annotation { "Feature Type Name" : "Feature", "Feature Type Description" : "" }
export const myFeature = defineFeature(function(context is Context, id is Id, definition is map)
    precondition{}
    {
        {
            var Q0;
            Q0=qCreatedBy(makeId("Top.planeOp"),FACE);
            var sketch = newSketch(context, id + "F0", { "sketchPlane" : qUnion([Q0])});
            skLineSegment(sketch, "E0.bottom", {"start": v(0, 0) * mm, "end": v(2000, 0) * mm});
            skLineSegment(sketch, "E0.top", {"start": v(0, 2000) * mm, "end": v(2000, 2000) * mm});
            skLineSegment(sketch, "E0.left", {"start": v(0, 0) * mm, "end": v(0, 2000) * mm});
            skLineSegment(sketch, "E0.right", {"start": v(2000, 0) * mm, "end": v(2000, 2000) * mm});
            skSolve(sketch);
        }
        {
            var Q0;
            Q0=makeQuery(id+"F0.imprint","IMPRINT",FACE,{"disambiguationData":[TD([[makeQuery(id+"F0.imprint","IMPRINT",EDGE,{"derivedFrom":sQuery(id+"F0.wireOp",EDGE,"E0.bottom")}),1.0]])]});
            extrude(context, id + "F1", {"entities" : qUnion([Q0]), "oppositeDirection" : true, "depth" : 500 * mm, "offsetDistance" : 25 * mm});
        }
        {
            var Q0;
            Q0=makeQuery(id+"F1.opExtrude","CAP_FACE",FACE,{"disambiguationData":[OSD([sQuery(id+"F0.wireOp",EDGE,"E0.bottom"),sQuery(id+"F0.wireOp",EDGE,"E0.top"),sQuery(id+"F0.wireOp",EDGE,"E0.left"),sQuery(id+"F0.wireOp",EDGE,"E0.right")])],"isStart":true});
            cPlane(context, id + "F2", {"entities" : qUnion([Q0]), "cplaneType" : CPlaneType.OFFSET, "offset" : 1500 * mm, "width" : 150 * mm, "height" : 150 * mm});
        }
        {
            var Q0;
            Q0=qCreatedBy(id+"F2.planeOp",FACE);
            var sketch = newSketch(context, id + "F3", { "sketchPlane" : qUnion([Q0])});
            skLineSegment(sketch, "E1.bottom", {"start": v(0, 1500) * mm, "end": v(2000, 1500) * mm});
            skLineSegment(sketch, "E1.top", {"start": v(0, -500) * mm, "end": v(2000, -500) * mm});
            skLineSegment(sketch, "E1.left", {"start": v(0, 1500) * mm, "end": v(0, -500) * mm});
            skLineSegment(sketch, "E1.right", {"start": v(2000, 1500) * mm, "end": v(2000, -500) * mm});
            skSolve(sketch);
        }
        {
            var Q1;
            Q1=makeQuery(id+"F3.imprint","IMPRINT",FACE,{"disambiguationData":[TD([[makeQuery(id+"F3.imprint","IMPRINT",EDGE,{"derivedFrom":sQuery(id+"F3.wireOp",EDGE,"E1.bottom")}),-1.0]])]});
            var Q2;
            Q2=makeQuery(id+"F1.opExtrude","CAP_FACE",FACE,{"disambiguationData":[OSD([sQuery(id+"F0.wireOp",EDGE,"E0.bottom"),sQuery(id+"F0.wireOp",EDGE,"E0.top"),sQuery(id+"F0.wireOp",EDGE,"E0.left"),sQuery(id+"F0.wireOp",EDGE,"E0.right")])],"isStart":true});
            loft(context, id + "F4", {"operationType" : NewBodyOperationType.ADD, "sheetProfilesArray" : [{ "sheetProfileEntities" : qUnion([Q1]) }, { "sheetProfileEntities" : qUnion([Q2]) }]});
        }
        {
            var Q0;
            Q0=makeQuery(id+"F1.opExtrude","CAP_FACE",FACE,{"disambiguationData":[OSD([sQuery(id+"F0.wireOp",EDGE,"E0.bottom"),sQuery(id+"F0.wireOp",EDGE,"E0.top"),sQuery(id+"F0.wireOp",EDGE,"E0.left"),sQuery(id+"F0.wireOp",EDGE,"E0.right")])],"isStart":false});
            cPlane(context, id + "F5", {"entities" : qUnion([Q0]), "cplaneType" : CPlaneType.OFFSET, "offset" : 1200 * mm, "width" : 150 * mm, "height" : 150 * mm});
        }
        {
            var Q0;
            Q0=qCreatedBy(id+"F5.planeOp",FACE);
            var sketch = newSketch(context, id + "F6", { "sketchPlane" : qUnion([Q0])});
            skLineSegment(sketch, "E2.bottom", {"start": v(900, -900) * mm, "end": v(1100, -900) * mm});
            skLineSegment(sketch, "E2.top", {"start": v(900, -1100) * mm, "end": v(1100, -1100) * mm});
            skLineSegment(sketch, "E2.left", {"start": v(900, -900) * mm, "end": v(900, -1100) * mm});
            skLineSegment(sketch, "E2.right", {"start": v(1100, -900) * mm, "end": v(1100, -1100) * mm});
            skSolve(sketch);
        }
        {
            var Q1;
            Q1=makeQuery(id+"F1.opExtrude","CAP_FACE",FACE,{"disambiguationData":[OSD([sQuery(id+"F0.wireOp",EDGE,"E0.bottom"),sQuery(id+"F0.wireOp",EDGE,"E0.top"),sQuery(id+"F0.wireOp",EDGE,"E0.left"),sQuery(id+"F0.wireOp",EDGE,"E0.right")])],"isStart":false});
            var Q2;
            Q2=makeQuery(id+"F6.imprint","IMPRINT",FACE,{"disambiguationData":[TD([[makeQuery(id+"F6.imprint","IMPRINT",EDGE,{"derivedFrom":sQuery(id+"F6.wireOp",EDGE,"E2.bottom")}),-1.0]])]});
            loft(context, id + "F7", {"operationType" : NewBodyOperationType.ADD, "sheetProfilesArray" : [{ "sheetProfileEntities" : qUnion([Q1]) }, { "sheetProfileEntities" : qUnion([Q2]) }]});
        }
        {
            var Q0;
            Q0=makeQuery(id+"F4.opLoft","CAP_FACE",FACE,{"disambiguationData":[OSD([makeQuery(id+"F3.imprint","IMPRINT",FACE,{"disambiguationData":[TD([[makeQuery(id+"F3.imprint","IMPRINT",EDGE,{"derivedFrom":sQuery(id+"F3.wireOp",EDGE,"E1.bottom")}),-1.0]])]})])],"isStart":true});
            var sketch = newSketch(context, id + "F8", { "sketchPlane" : qUnion([Q0])});
            skLineSegment(sketch, "E3.bottom", {"start": v(2000, -500) * mm, "end": v(0, -500) * mm});
            skLineSegment(sketch, "E3.top", {"start": v(2000, 1800) * mm, "end": v(0, 1800) * mm});
            skLineSegment(sketch, "E3.left", {"start": v(2000, -500) * mm, "end": v(2000, 1800) * mm});
            skLineSegment(sketch, "E3.right", {"start": v(0, -500) * mm, "end": v(0, 1800) * mm});
            skSolve(sketch);
        }
        {
            var Q0;
            Q0 = qSketchRegion(id + "F8", true);
            extrude(context, id + "F9", {"entities" : qUnion([Q0]), "operationType" : NewBodyOperationType.ADD, "depth" : 300 * mm, "offsetDistance" : 25 * mm});
        }
        {
            var Q0;
            Q0=makeQuery(id+"F9.opExtrude","SWEPT_FACE",FACE,{"disambiguationData":[OSD([sQuery(id+"F8.wireOp",EDGE,"E3.top")])]});
            var sketch = newSketch(context, id + "F10", { "sketchPlane" : qUnion([Q0])});
            skCircle(sketch, "E4", {"center": v(-1000, 1650) * mm, "radius": 50 * mm});
            skPoint(sketch, "E4.centerSnap0", {"position": v(-1000, 1800) * mm});
            skSolve(sketch);
        }
        {
            var Q0;
            Q0=makeQuery(id+"F10.imprint","IMPRINT",FACE,{"disambiguationData":[TD([[makeQuery(id+"F10.imprint","IMPRINT",EDGE,{"derivedFrom":sQuery(id+"F10.wireOp",EDGE,"E4")}),1.0]])]});
            var Q1;
            Q1=sQuery(id+"F10.wireOp",EDGE,"E4");
            extrude(context, id + "F11", {"entities" : qUnion([Q0]), "operationType" : NewBodyOperationType.ADD, "surfaceEntities" : qUnion([Q1]), "depth" : 100 * mm, "offsetDistance" : 25 * mm});
        }
        {
            var Q0;
            Q0=makeQuery(id+"F11.opExtrude","CAP_FACE",FACE,{"disambiguationData":[OSD([sQuery(id+"F10.wireOp",EDGE,"E4")])],"isStart":false});
            var sketch = newSketch(context, id + "F12", { "sketchPlane" : qUnion([Q0])});
            skCircle(sketch, "E5", {"center": v(-1000, 1650) * mm, "radius": 115 * mm});
            skCircle(sketch, "E6", {"center": v(-1000, 1745) * mm, "radius": 9 * mm});
            skCircle(sketch, "E7.1.0", {"center": v(-1067.18, 1717.18) * mm, "radius": 9 * mm});
            skCircle(sketch, "E7.2.0", {"center": v(-1095, 1650) * mm, "radius": 9 * mm});
            skCircle(sketch, "E7.3.0", {"center": v(-1067.18, 1582.82) * mm, "radius": 9 * mm});
            skCircle(sketch, "E7.4.0", {"center": v(-1000, 1555) * mm, "radius": 9 * mm});
            skCircle(sketch, "E7.5.0", {"center": v(-932.82, 1582.82) * mm, "radius": 9 * mm});
            skCircle(sketch, "E7.6.0", {"center": v(-905, 1650) * mm, "radius": 9 * mm});
            skCircle(sketch, "E7.7.0", {"center": v(-932.82, 1717.18) * mm, "radius": 9 * mm});
            skSolve(sketch);
        }
        {
            var Q0;
            Q0=makeQuery(id+"F12.imprint","IMPRINT",FACE,{"disambiguationData":[TD([[makeQuery(id+"F12.imprint","IMPRINT",EDGE,{"derivedFrom":sQuery(id+"F12.wireOp",EDGE,"E5")}),1.0]])]});
            extrude(context, id + "F13", {"entities" : qUnion([Q0]), "operationType" : NewBodyOperationType.ADD, "oppositeDirection" : true, "depth" : 25 * mm, "offsetDistance" : 25 * mm});
        }
        {
            var Q0;
            {var subQ0=sQuery(id+"F10.wireOp",EDGE,"E4");Q0=makeQuery(id+"F13.boolean.opBoolean","MERGE",FACE,{"derivedFrom":[makeQuery(id+"F11.opExtrude","CAP_FACE",FACE,{"disambiguationData":[OSD([subQ0])],"isStart":false}),makeQuery(id+"F13.opExtrude","CAP_FACE",FACE,{"disambiguationData":[OSD([subQ0,sQuery(id+"F12.wireOp",EDGE,"E5"),sQuery(id+"F12.wireOp",EDGE,"E6"),sQuery(id+"F12.wireOp",EDGE,"E7.1.0"),sQuery(id+"F12.wireOp",EDGE,"E7.2.0"),sQuery(id+"F12.wireOp",EDGE,"E7.3.0"),sQuery(id+"F12.wireOp",EDGE,"E7.4.0"),sQuery(id+"F12.wireOp",EDGE,"E7.5.0"),sQuery(id+"F12.wireOp",EDGE,"E7.6.0"),sQuery(id+"F12.wireOp",EDGE,"E7.7.0")])],"isStart":true})]});}
            var sketch = newSketch(context, id + "F14", { "sketchPlane" : qUnion([Q0])});
            skCircle(sketch, "E8", {"center": v(-1000, 1650) * mm, "radius": 40 * mm});
            skSolve(sketch);
        }
        {
            var Q0;
            Q0=makeQuery(id+"F14.imprint","IMPRINT",FACE,{"disambiguationData":[TD([[makeQuery(id+"F14.imprint","IMPRINT",EDGE,{"derivedFrom":sQuery(id+"F14.wireOp",EDGE,"E8")}),1.0]])]});
            extrude(context, id + "F15", {"entities" : qUnion([Q0]), "operationType" : NewBodyOperationType.REMOVE, "oppositeDirection" : true, "depth" : 500 * mm, "offsetDistance" : 25 * mm});
        }
        {
            var Q0;
            Q0=makeQuery(id+"F1.opExtrude","SWEPT_FACE",FACE,{"disambiguationData":[OSD([sQuery(id+"F0.wireOp",EDGE,"E0.top")])]});
            var sketch = newSketch(context, id + "F16", { "sketchPlane" : qUnion([Q0])});
            skCircle(sketch, "E9", {"center": v(-1000, -250) * mm, "radius": 40 * mm});
            skCircle(sketch, "E10", {"center": v(-1000, -250) * mm, "radius": 50 * mm});
            skSolve(sketch);
        }
        {
            var Q0;
            Q0=makeQuery(id+"F16.imprint","IMPRINT",FACE,{"disambiguationData":[TD([[makeQuery(id+"F16.imprint","IMPRINT",EDGE,{"derivedFrom":sQuery(id+"F16.wireOp",EDGE,"E9")}),1.0]])]});
            extrude(context, id + "F17", {"entities" : qUnion([Q0]), "operationType" : NewBodyOperationType.REMOVE, "oppositeDirection" : true, "depth" : 25 * mm, "offsetDistance" : 25 * mm});
        }
        {
            var Q0;
            Q0 = qSketchRegion(id + "F16", true);
            extrude(context, id + "F18", {"entities" : qUnion([Q0]), "operationType" : NewBodyOperationType.ADD, "depth" : 100 * mm, "offsetDistance" : 25 * mm});
        }
        {
            var Q0;
            Q0=makeQuery(id+"F18.opExtrude","CAP_FACE",FACE,{"disambiguationData":[OSD([sQuery(id+"F16.wireOp",EDGE,"E9"),sQuery(id+"F16.wireOp",EDGE,"E10")])],"isStart":false});
            var sketch = newSketch(context, id + "F19", { "sketchPlane" : qUnion([Q0])});
            skCircle(sketch, "E11", {"center": v(-1000, -250) * mm, "radius": 100 * mm});
            skCircle(sketch, "E12", {"center": v(-1000, -173) * mm, "radius": 8 * mm});
            skCircle(sketch, "E13.1.0", {"center": v(-1054.45, -195.55) * mm, "radius": 8 * mm});
            skCircle(sketch, "E13.2.0", {"center": v(-1077, -250) * mm, "radius": 8 * mm});
            skCircle(sketch, "E13.3.0", {"center": v(-1054.45, -304.45) * mm, "radius": 8 * mm});
            skCircle(sketch, "E13.4.0", {"center": v(-1000, -327) * mm, "radius": 8 * mm});
            skCircle(sketch, "E13.5.0", {"center": v(-945.55, -304.45) * mm, "radius": 8 * mm});
            skCircle(sketch, "E13.6.0", {"center": v(-923, -250) * mm, "radius": 8 * mm});
            skCircle(sketch, "E13.7.0", {"center": v(-945.55, -195.55) * mm, "radius": 8 * mm});
            skSolve(sketch);
        }
        {
            var Q0;
            Q0=makeQuery(id+"F19.imprint","IMPRINT",FACE,{"disambiguationData":[TD([[makeQuery(id+"F19.imprint","IMPRINT",EDGE,{"derivedFrom":sQuery(id+"F19.wireOp",EDGE,"E11")}),1.0]])]});
            extrude(context, id + "F20", {"entities" : qUnion([Q0]), "operationType" : NewBodyOperationType.ADD, "oppositeDirection" : true, "depth" : 15 * mm, "offsetDistance" : 25 * mm});
        }
        {
            var Q0;
            {var subQ0=sQuery(id+"F0.wireOp",EDGE,"E0.left");Q0=makeQuery(id+"F9.boolean.opBoolean","MERGE",FACE,{"derivedFrom":[makeQuery(id+"F4.boolean.opBoolean","MERGE",FACE,{"derivedFrom":[makeQuery(id+"F1.opExtrude","SWEPT_FACE",FACE,{"disambiguationData":[OSD([subQ0])]}),makeQuery(id+"F4.opLoft","SWEPT_FACE",FACE,{"disambiguationData":[OSD([sQuery(id+"F0.wireOp",EDGE,"E0.bottom"),sQuery(id+"F0.wireOp",EDGE,"E0.top"),subQ0,sQuery(id+"F3.wireOp",EDGE,"E1.bottom"),sQuery(id+"F3.wireOp",EDGE,"E1.top"),sQuery(id+"F3.wireOp",EDGE,"E1.left")])]})]}),makeQuery(id+"F9.opExtrude","SWEPT_FACE",FACE,{"disambiguationData":[OSD([sQuery(id+"F8.wireOp",EDGE,"E3.right")])]})]});}
            var sketch = newSketch(context, id + "F21", { "sketchPlane" : qUnion([Q0])});
            skLineSegment(sketch, "E14.bottom", {"start": v(-2050, 0) * mm, "end": v(50, 0) * mm});
            skLineSegment(sketch, "E14.top", {"start": v(-2050, -10) * mm, "end": v(50, -10) * mm});
            skLineSegment(sketch, "E14.left", {"start": v(-2050, 0) * mm, "end": v(-2050, -10) * mm});
            skLineSegment(sketch, "E14.right", {"start": v(50, 0) * mm, "end": v(50, -10) * mm});
            skLineSegment(sketch, "E15.0.1.0", {"start": v(-2050, -490) * mm, "end": v(50, -490) * mm});
            skLineSegment(sketch, "E15.0.1.1", {"start": v(-2050, -500) * mm, "end": v(50, -500) * mm});
            skLineSegment(sketch, "E15.0.1.2", {"start": v(50, -490) * mm, "end": v(50, -500) * mm});
            skLineSegment(sketch, "E15.0.1.3", {"start": v(-2050, -490) * mm, "end": v(-2050, -500) * mm});
            skLineSegment(sketch, "E15.direction1", {"start": v(-2050, 0) * mm, "end": v(-2025, 0) * mm, "construction": true});
            skLineSegment(sketch, "E15.direction2", {"start": v(-2050, 0) * mm, "end": v(-2050, -490) * mm, "construction": true});
            skSolve(sketch);
        }
        {
            var Q0;
            Q0 = qSketchRegion(id + "F21", true);
            extrude(context, id + "F22", {"entities" : qUnion([Q0]), "operationType" : NewBodyOperationType.ADD, "oppositeDirection" : true, "depth" : 2050 * mm, "offsetDistance" : 25 * mm, "hasSecondDirection" : true, "secondDirectionOppositeDirection" : false, "secondDirectionDepth" : 50 * mm});
        }
        {
            var Q0;
            {var subQ0=sQuery(id+"F8.wireOp",EDGE,"E3.bottom");var subQ2=sQuery(id+"F3.wireOp",EDGE,"E1.left");var subQ3=sQuery(id+"F3.wireOp",EDGE,"E1.bottom");var subQ5=sQuery(id+"F0.wireOp",EDGE,"E0.left");var subQ6=sQuery(id+"F0.wireOp",EDGE,"E0.top");var subQ7=sQuery(id+"F8.wireOp",EDGE,"E3.right");var subQ10=sQuery(id+"F3.wireOp",EDGE,"E1.top");var subQ11=sQuery(id+"F0.wireOp",EDGE,"E0.bottom");Q0=makeQuery(id+"F22.boolean.opBoolean","SPLIT",FACE,{"disambiguationData":[TD([makeQuery(id+"F9.opExtrude","SWEPT_FACE",FACE,{"disambiguationData":[OSD([subQ0])]})])],"derivedFrom":makeQuery(id+"F9.boolean.opBoolean","MERGE",FACE,{"derivedFrom":[makeQuery(id+"F4.boolean.opBoolean","MERGE",FACE,{"derivedFrom":[makeQuery(id+"F1.opExtrude","SWEPT_FACE",FACE,{"disambiguationData":[OSD([subQ5])]}),makeQuery(id+"F4.opLoft","SWEPT_FACE",FACE,{"disambiguationData":[OSD([subQ11,subQ6,subQ5,subQ3,subQ10,subQ2])]})]}),makeQuery(id+"F9.opExtrude","SWEPT_FACE",FACE,{"disambiguationData":[OSD([subQ7])]})]})});}
            var sketch = newSketch(context, id + "F23", { "sketchPlane" : qUnion([Q0])});
            skLineSegment(sketch, "E16.0", {"start": v(-1500, 1500) * mm, "end": v(-2000, 0) * mm});
            skLineSegment(sketch, "E17", {"start": v(-1500, 1500) * mm, "end": v(-1480, 1500) * mm});
            skLineSegment(sketch, "E18", {"start": v(-1480, 1500) * mm, "end": v(-1980, 0) * mm});
            skLineSegment(sketch, "E19", {"start": v(-1980, 0) * mm, "end": v(-2000, 0) * mm});
            skLineSegment(sketch, "E20.1.0.0", {"start": v(-820, 1500) * mm, "end": v(-1320, 0) * mm});
            skLineSegment(sketch, "E20.1.0.1", {"start": v(-840, 1500) * mm, "end": v(-1340, 0) * mm});
            skLineSegment(sketch, "E20.1.0.2", {"start": v(-840, 1500) * mm, "end": v(-820, 1500) * mm});
            skLineSegment(sketch, "E20.1.0.3", {"start": v(-1320, 0) * mm, "end": v(-1340, 0) * mm});
            skLineSegment(sketch, "E20.2.0.0", {"start": v(-160, 1500) * mm, "end": v(-660, 0) * mm});
            skLineSegment(sketch, "E20.2.0.1", {"start": v(-180, 1500) * mm, "end": v(-680, 0) * mm});
            skLineSegment(sketch, "E20.2.0.2", {"start": v(-180, 1500) * mm, "end": v(-160, 1500) * mm});
            skLineSegment(sketch, "E20.2.0.3", {"start": v(-660, 0) * mm, "end": v(-680, 0) * mm});
            skLineSegment(sketch, "E20.3.0.0", {"start": v(500, 1500) * mm, "end": v(0, 0) * mm});
            skLineSegment(sketch, "E20.3.0.1", {"start": v(480, 1500) * mm, "end": v(-20, 0) * mm});
            skLineSegment(sketch, "E20.3.0.2", {"start": v(480, 1500) * mm, "end": v(500, 1500) * mm});
            skLineSegment(sketch, "E20.3.0.3", {"start": v(0, 0) * mm, "end": v(-20, 0) * mm});
            skLineSegment(sketch, "E20.direction1", {"start": v(-1980, 0) * mm, "end": v(-1320, 0) * mm, "construction": true});
            skSolve(sketch);
        }
        {
            var Q0;
            Q0 = qSketchRegion(id + "F23", true);
            extrude(context, id + "F24", {"entities" : qUnion([Q0]), "operationType" : NewBodyOperationType.ADD, "oppositeDirection" : true, "depth" : 2050 * mm, "offsetDistance" : 25 * mm, "hasSecondDirection" : true, "secondDirectionOppositeDirection" : false, "secondDirectionDepth" : 50 * mm});
        }
        {
            var Q0;
            {var subQ0=sQuery(id+"F8.wireOp",EDGE,"E3.bottom");var subQ2=sQuery(id+"F3.wireOp",EDGE,"E1.left");var subQ3=sQuery(id+"F3.wireOp",EDGE,"E1.bottom");var subQ5=sQuery(id+"F0.wireOp",EDGE,"E0.left");var subQ6=sQuery(id+"F0.wireOp",EDGE,"E0.top");var subQ7=sQuery(id+"F8.wireOp",EDGE,"E3.right");var subQ10=sQuery(id+"F3.wireOp",EDGE,"E1.top");var subQ11=sQuery(id+"F0.wireOp",EDGE,"E0.bottom");Q0=makeQuery(id+"F22.boolean.opBoolean","SPLIT",FACE,{"disambiguationData":[TD([makeQuery(id+"F9.opExtrude","SWEPT_FACE",FACE,{"disambiguationData":[OSD([subQ0])]})])],"derivedFrom":makeQuery(id+"F9.boolean.opBoolean","MERGE",FACE,{"derivedFrom":[makeQuery(id+"F4.boolean.opBoolean","MERGE",FACE,{"derivedFrom":[makeQuery(id+"F1.opExtrude","SWEPT_FACE",FACE,{"disambiguationData":[OSD([subQ5])]}),makeQuery(id+"F4.opLoft","SWEPT_FACE",FACE,{"disambiguationData":[OSD([subQ11,subQ6,subQ5,subQ3,subQ10,subQ2])]})]}),makeQuery(id+"F9.opExtrude","SWEPT_FACE",FACE,{"disambiguationData":[OSD([subQ7])]})]})});}
            var sketch = newSketch(context, id + "F25", { "sketchPlane" : qUnion([Q0])});
            skLineSegment(sketch, "E21.bottom", {"start": v(500, 1500) * mm, "end": v(-1850, 1500) * mm});
            skLineSegment(sketch, "E21.top", {"start": v(500, 1520) * mm, "end": v(-1850, 1520) * mm});
            skLineSegment(sketch, "E21.left", {"start": v(500, 1500) * mm, "end": v(500, 1520) * mm});
            skLineSegment(sketch, "E21.right", {"start": v(-1850, 1500) * mm, "end": v(-1850, 1520) * mm});
            skSolve(sketch);
        }
        {
            var Q0;
            Q0 = qSketchRegion(id + "F25", true);
            extrude(context, id + "F26", {"entities" : qUnion([Q0]), "operationType" : NewBodyOperationType.ADD, "oppositeDirection" : true, "depth" : 2050 * mm, "offsetDistance" : 25 * mm, "hasSecondDirection" : true, "secondDirectionOppositeDirection" : false, "secondDirectionDepth" : 50 * mm});
        }
        {
            var Q0;
            Q0=makeQuery(id+"F7.opLoft","CAP_FACE",FACE,{"disambiguationData":[OSD([makeQuery(id+"F6.imprint","IMPRINT",FACE,{"disambiguationData":[TD([[makeQuery(id+"F6.imprint","IMPRINT",EDGE,{"derivedFrom":sQuery(id+"F6.wireOp",EDGE,"E2.bottom")}),-1.0]])]})])],"isStart":true});
            cPlane(context, id + "F27", {"entities" : qUnion([Q0]), "cplaneType" : CPlaneType.OFFSET, "offset" : 400 * mm, "oppositeDirection" : true, "width" : 150 * mm, "height" : 150 * mm});
        }
        {
            var Q0;
            Q0=makeQuery(id+"F7.opLoft","CAP_FACE",FACE,{"disambiguationData":[OSD([makeQuery(id+"F6.imprint","IMPRINT",FACE,{"disambiguationData":[TD([[makeQuery(id+"F6.imprint","IMPRINT",EDGE,{"derivedFrom":sQuery(id+"F6.wireOp",EDGE,"E2.bottom")}),-1.0]])]})])],"isStart":true});
            cPlane(context, id + "F28", {"entities" : qUnion([Q0]), "cplaneType" : CPlaneType.OFFSET, "offset" : 800 * mm, "oppositeDirection" : true, "width" : 150 * mm, "height" : 150 * mm});
        }
        {
            var Q0;
            Q0=qCreatedBy(id+"F27.planeOp",FACE);
            var sketch = newSketch(context, id + "F29", { "sketchPlane" : qUnion([Q0])});
            skLineSegment(sketch, "E22.bottom", {"start": v(503.12, -1496.88) * mm, "end": v(1503.12, -1496.88) * mm});
            skLineSegment(sketch, "E22.top", {"start": v(503.12, -496.88) * mm, "end": v(1503.12, -496.88) * mm});
            skLineSegment(sketch, "E22.left", {"start": v(503.12, -1496.88) * mm, "end": v(503.12, -496.88) * mm});
            skLineSegment(sketch, "E22.right", {"start": v(1503.12, -1496.88) * mm, "end": v(1503.12, -496.88) * mm});
            skLineSegment(sketch, "E23.0", {"start": v(0, -2000) * mm, "end": v(900, -1100) * mm});
            skLineSegment(sketch, "E24.0", {"start": v(0, 0) * mm, "end": v(900, -900) * mm});
            skSolve(sketch);
        }
        {
            var Q0;
            Q0 = qSketchRegion(id + "F29", true);
            extrude(context, id + "F30", {"entities" : qUnion([Q0]), "operationType" : NewBodyOperationType.ADD, "oppositeDirection" : true, "depth" : 25 * mm, "offsetDistance" : 25 * mm});
        }
        {
            var Q0;
            Q0=qCreatedBy(id+"F28.planeOp",FACE);
            var sketch = newSketch(context, id + "F31", { "sketchPlane" : qUnion([Q0])});
            skLineSegment(sketch, "E25.bottom", {"start": v(251.64, -1748.81) * mm, "end": v(1751.64, -1748.81) * mm});
            skLineSegment(sketch, "E25.top", {"start": v(251.64, -248.81) * mm, "end": v(1751.64, -248.81) * mm});
            skLineSegment(sketch, "E25.left", {"start": v(251.64, -1748.81) * mm, "end": v(251.64, -248.81) * mm});
            skLineSegment(sketch, "E25.right", {"start": v(1751.64, -1748.81) * mm, "end": v(1751.64, -248.81) * mm});
            skSolve(sketch);
        }
        {
            var Q0;
            Q0 = qSketchRegion(id + "F31", true);
            extrude(context, id + "F32", {"entities" : qUnion([Q0]), "operationType" : NewBodyOperationType.ADD, "depth" : 25 * mm, "offsetDistance" : 25 * mm});
        }
        {
            var Q0;
            Q0=makeQuery(id+"F22.opExtrude","SWEPT_FACE",FACE,{"disambiguationData":[OSD([sQuery(id+"F21.wireOp",EDGE,"E15.0.1.1")])]});
            var sketch = newSketch(context, id + "F33", { "sketchPlane" : qUnion([Q0])});
            skLineSegment(sketch, "E26.bottom", {"start": v(-50, -2050) * mm, "end": v(70, -2050) * mm});
            skLineSegment(sketch, "E26.top", {"start": v(-50, -1930) * mm, "end": v(70, -1930) * mm});
            skLineSegment(sketch, "E26.left", {"start": v(-50, -2050) * mm, "end": v(-50, -1930) * mm});
            skLineSegment(sketch, "E26.right", {"start": v(70, -2050) * mm, "end": v(70, -1930) * mm});
            skLineSegment(sketch, "E27.0.1.0", {"start": v(-50, 50) * mm, "end": v(70, 50) * mm});
            skLineSegment(sketch, "E27.0.1.1", {"start": v(70, -70) * mm, "end": v(70, 50) * mm});
            skLineSegment(sketch, "E27.0.1.2", {"start": v(-50, -70) * mm, "end": v(70, -70) * mm});
            skLineSegment(sketch, "E27.0.1.3", {"start": v(-50, -70) * mm, "end": v(-50, 50) * mm});
            skLineSegment(sketch, "E27.1.0.0", {"start": v(1930, -1930) * mm, "end": v(2050, -1930) * mm});
            skLineSegment(sketch, "E27.1.0.1", {"start": v(2050, -2050) * mm, "end": v(2050, -1930) * mm});
            skLineSegment(sketch, "E27.1.0.2", {"start": v(1930, -2050) * mm, "end": v(2050, -2050) * mm});
            skLineSegment(sketch, "E27.1.0.3", {"start": v(1930, -2050) * mm, "end": v(1930, -1930) * mm});
            skLineSegment(sketch, "E27.1.1.0", {"start": v(1930, 50) * mm, "end": v(2050, 50) * mm});
            skLineSegment(sketch, "E27.1.1.1", {"start": v(2050, -70) * mm, "end": v(2050, 50) * mm});
            skLineSegment(sketch, "E27.1.1.2", {"start": v(1930, -70) * mm, "end": v(2050, -70) * mm});
            skLineSegment(sketch, "E27.1.1.3", {"start": v(1930, -70) * mm, "end": v(1930, 50) * mm});
            skLineSegment(sketch, "E27.direction1", {"start": v(-50, -1930) * mm, "end": v(1930, -1930) * mm, "construction": true});
            skLineSegment(sketch, "E27.direction2", {"start": v(-50, -1930) * mm, "end": v(-50, 50) * mm, "construction": true});
            skSolve(sketch);
        }
        {
            var Q0;
            Q0 = qSketchRegion(id + "F33", true);
            extrude(context, id + "F34", {"entities" : qUnion([Q0]), "operationType" : NewBodyOperationType.ADD, "depth" : 1800 * mm, "offsetDistance" : 25 * mm});
        }
        {
            var Q0;
            Q0=makeQuery(id+"F7.opLoft","CAP_FACE",FACE,{"disambiguationData":[OSD([makeQuery(id+"F6.imprint","IMPRINT",FACE,{"disambiguationData":[TD([[makeQuery(id+"F6.imprint","IMPRINT",EDGE,{"derivedFrom":sQuery(id+"F6.wireOp",EDGE,"E2.bottom")}),-1.0]])]})])],"isStart":true});
            var sketch = newSketch(context, id + "F35", { "sketchPlane" : qUnion([Q0])});
            skLineSegment(sketch, "E28.bottom", {"start": v(900, -1100) * mm, "end": v(1100, -1100) * mm});
            skLineSegment(sketch, "E28.top", {"start": v(900, -900) * mm, "end": v(1100, -900) * mm});
            skLineSegment(sketch, "E28.left", {"start": v(900, -1100) * mm, "end": v(900, -900) * mm});
            skLineSegment(sketch, "E28.right", {"start": v(1100, -1100) * mm, "end": v(1100, -900) * mm});
            skSolve(sketch);
        }
        {
            var Q0;
            Q0=makeQuery(id+"F35.imprint","IMPRINT",FACE,{"disambiguationData":[TD([[makeQuery(id+"F35.imprint","IMPRINT",EDGE,{"derivedFrom":sQuery(id+"F35.wireOp",EDGE,"E28.bottom")}),1.0]])]});
            extrude(context, id + "F36", {"entities" : qUnion([Q0]), "operationType" : NewBodyOperationType.ADD, "depth" : 200 * mm, "offsetDistance" : 25 * mm});
        }
        {
            var Q0;
            Q0=makeQuery(id+"F36.opExtrude","SWEPT_FACE",FACE,{"disambiguationData":[OSD([sQuery(id+"F35.wireOp",EDGE,"E28.top")])]});
            var sketch = newSketch(context, id + "F37", { "sketchPlane" : qUnion([Q0])});
            skCircle(sketch, "E29", {"center": v(1000, -1800) * mm, "radius": 40 * mm});
            skPoint(sketch, "E29.centerSnap0", {"position": v(900, -1800) * mm});
            skCircle(sketch, "E30", {"center": v(1000, -1800) * mm, "radius": 50 * mm});
            skSolve(sketch);
        }
        {
            var Q0;
            Q0 = qSketchRegion(id + "F37", true);
            extrude(context, id + "F38", {"entities" : qUnion([Q0]), "operationType" : NewBodyOperationType.ADD, "depth" : 100 * mm, "offsetDistance" : 25 * mm});
        }
        {
            var Q0;
            Q0=makeQuery(id+"F38.opExtrude","CAP_FACE",FACE,{"disambiguationData":[OSD([sQuery(id+"F37.wireOp",EDGE,"E29"),sQuery(id+"F37.wireOp",EDGE,"E30")])],"isStart":false});
            var sketch = newSketch(context, id + "F39", { "sketchPlane" : qUnion([Q0])});
            skCircle(sketch, "E31", {"center": v(1000, -1800) * mm, "radius": 82.5 * mm});
            skSolve(sketch);
        }
        {
            var Q0;
            Q0=makeQuery(id+"F39.imprint","IMPRINT",FACE,{"disambiguationData":[TD([[makeQuery(id+"F39.imprint","IMPRINT",EDGE,{"derivedFrom":sQuery(id+"F39.wireOp",EDGE,"E31")}),1.0]])]});
            extrude(context, id + "F40", {"entities" : qUnion([Q0]), "operationType" : NewBodyOperationType.ADD, "oppositeDirection" : true, "depth" : 15 * mm, "offsetDistance" : 25 * mm});
        }
        {
            var Q0;
            {var subQ0=sQuery(id+"F0.wireOp",EDGE,"E0.bottom");var subQ1=sQuery(id+"F0.wireOp",EDGE,"E0.top");var subQ2=sQuery(id+"F0.wireOp",EDGE,"E0.left");Q0=makeQuery(id+"F22.boolean.opBoolean","SPLIT",FACE,{"disambiguationData":[TD([makeQuery(id+"F1.opExtrude","SWEPT_FACE",FACE,{"disambiguationData":[OSD([subQ0])]})])],"derivedFrom":makeQuery(id+"F9.boolean.opBoolean","MERGE",FACE,{"derivedFrom":[makeQuery(id+"F4.boolean.opBoolean","MERGE",FACE,{"derivedFrom":[makeQuery(id+"F1.opExtrude","SWEPT_FACE",FACE,{"disambiguationData":[OSD([subQ2])]}),makeQuery(id+"F4.opLoft","SWEPT_FACE",FACE,{"disambiguationData":[OSD([subQ0,subQ1,subQ2,sQuery(id+"F3.wireOp",EDGE,"E1.bottom"),sQuery(id+"F3.wireOp",EDGE,"E1.top"),sQuery(id+"F3.wireOp",EDGE,"E1.left")])]})]}),makeQuery(id+"F9.opExtrude","SWEPT_FACE",FACE,{"disambiguationData":[OSD([sQuery(id+"F8.wireOp",EDGE,"E3.right")])]})]})});}
            var sketch = newSketch(context, id + "F41", { "sketchPlane" : qUnion([Q0])});
            skText(sketch, "E32", { "text": "Separtation Technology", "fontName": "OpenSans-Regular.ttf"});
            const initialGuessF41  = {"E32": [-2, -0.34024, 1, 0, 0.13056]};
            skSetInitialGuess(sketch, initialGuessF41);
            skSolve(sketch);
        }
        {
            var Q0;
            {var subQ0=sQuery(id+"F0.wireOp",EDGE,"E0.bottom");var subQ1=sQuery(id+"F0.wireOp",EDGE,"E0.top");var subQ2=sQuery(id+"F0.wireOp",EDGE,"E0.right");Q0=makeQuery(id+"F22.boolean.opBoolean","SPLIT",FACE,{"disambiguationData":[TD([makeQuery(id+"F1.opExtrude","SWEPT_FACE",FACE,{"disambiguationData":[OSD([subQ0])]})])],"derivedFrom":makeQuery(id+"F9.boolean.opBoolean","MERGE",FACE,{"derivedFrom":[makeQuery(id+"F4.boolean.opBoolean","MERGE",FACE,{"derivedFrom":[makeQuery(id+"F1.opExtrude","SWEPT_FACE",FACE,{"disambiguationData":[OSD([subQ2])]}),makeQuery(id+"F4.opLoft","SWEPT_FACE",FACE,{"disambiguationData":[OSD([subQ0,subQ1,subQ2,sQuery(id+"F3.wireOp",EDGE,"E1.bottom"),sQuery(id+"F3.wireOp",EDGE,"E1.top"),sQuery(id+"F3.wireOp",EDGE,"E1.right")])]})]}),makeQuery(id+"F9.opExtrude","SWEPT_FACE",FACE,{"disambiguationData":[OSD([sQuery(id+"F8.wireOp",EDGE,"E3.left")])]})]})});}
            var sketch = newSketch(context, id + "F42", { "sketchPlane" : qUnion([Q0])});
            skText(sketch, "E33", { "text": "Separation Technology", "fontName": "OpenSans-Regular.ttf"});
            const initialGuessF42  = {"E33": [0, -0.29825, 1, 0, 0.13326]};
            skSetInitialGuess(sketch, initialGuessF42);
            skSolve(sketch);
        }
        {
            var Q0;
            Q0=makeQuery(id+"F26.boolean.opBoolean","MERGE",FACE,{"derivedFrom":[makeQuery(id+"F9.opExtrude","SWEPT_FACE",FACE,{"disambiguationData":[OSD([sQuery(id+"F8.wireOp",EDGE,"E3.bottom")])]}),makeQuery(id+"F26.opExtrude","SWEPT_FACE",FACE,{"disambiguationData":[OSD([sQuery(id+"F25.wireOp",EDGE,"E21.left")])]})]});
            var sketch = newSketch(context, id + "F43", { "sketchPlane" : qUnion([Q0])});
            skLineSegment(sketch, "E34.bottom", {"start": v(0, 1800) * mm, "end": v(2000, 1800) * mm});
            skLineSegment(sketch, "E34.top", {"start": v(0, 1520) * mm, "end": v(2000, 1520) * mm});
            skLineSegment(sketch, "E34.left", {"start": v(0, 1800) * mm, "end": v(0, 1520) * mm});
            skLineSegment(sketch, "E34.right", {"start": v(2000, 1800) * mm, "end": v(2000, 1520) * mm});
            skSolve(sketch);
        }
        {
            var Q0;
            Q0=makeQuery(id+"F43.imprint","IMPRINT",FACE,{"disambiguationData":[TD([[makeQuery(id+"F43.imprint","IMPRINT",EDGE,{"derivedFrom":sQuery(id+"F43.wireOp",EDGE,"E34.bottom")}),1.0]])]});
            extrude(context, id + "F44", {"entities" : qUnion([Q0]), "operationType" : NewBodyOperationType.ADD, "depth" : 300 * mm, "offsetDistance" : 25 * mm});
        }
        {
            var Q0;
            Q0=makeQuery(id+"F44.opExtrude","SWEPT_FACE",FACE,{"disambiguationData":[OSD([sQuery(id+"F43.wireOp",EDGE,"E34.top")])]});
            var sketch = newSketch(context, id + "F45", { "sketchPlane" : qUnion([Q0])});
            skCircle(sketch, "E35", {"center": v(1000, 658.05) * mm, "radius": 50 * mm});
            skPoint(sketch, "E35.centerSnap0", {"position": v(1000, 800) * mm});
            skCircle(sketch, "E36", {"center": v(1000, 658.05) * mm, "radius": 60 * mm});
            skSolve(sketch);
        }
        {
            var Q0;
            Q0 = qSketchRegion(id + "F45", true);
            extrude(context, id + "F46", {"entities" : qUnion([Q0]), "operationType" : NewBodyOperationType.ADD, "depth" : 100 * mm, "offsetDistance" : 25 * mm});
        }
        {
            var Q0;
            Q0=makeQuery(id+"F46.opExtrude","CAP_FACE",FACE,{"disambiguationData":[OSD([sQuery(id+"F45.wireOp",EDGE,"E35"),sQuery(id+"F45.wireOp",EDGE,"E36")])],"isStart":false});
            var sketch = newSketch(context, id + "F47", { "sketchPlane" : qUnion([Q0])});
            skCircle(sketch, "E37", {"center": v(1000, 658.05) * mm, "radius": 125 * mm});
            skSolve(sketch);
        }
        {
            var Q0;
            Q0=makeQuery(id+"F47.imprint","IMPRINT",FACE,{"disambiguationData":[TD([[makeQuery(id+"F47.imprint","IMPRINT",EDGE,{"derivedFrom":sQuery(id+"F47.wireOp",EDGE,"E37")}),1.0]])]});
            extrude(context, id + "F48", {"entities" : qUnion([Q0]), "operationType" : NewBodyOperationType.ADD, "oppositeDirection" : true, "depth" : 20 * mm, "offsetDistance" : 25 * mm});
        }
    });